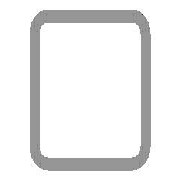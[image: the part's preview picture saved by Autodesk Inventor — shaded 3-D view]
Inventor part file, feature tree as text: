
AUTODESK INVENTOR PART (.ipt)
format: ipt  version: 2025.3 (Build 293356030, 356C)  size: 151,040 bytes
history: native  units: mm (DEFAULTED — no unit token found)
features: other x4, plane x3, split x2, sketch x1
ambient origin geometry x8: Origin, YZ Plane, XZ Plane, XY Plane, X Axis, Y Axis, Z Axis, Center Point
bodies: Solid1 (feature_tree), Body (feature_tree)
feature tree (10):
  parser-record x1  (decoder bookkeeping rows leaked as tree rows — omitted from the tree; the rows remain in map.json)
  other  "Driven Length"
  other  "Start Plane"
  other  "End Plane"
  plane  "Work Plane4"
  split  "Split1"
  plane  "Work Plane5"
  split  "Split2"
  sketch  "Sketch3"  dims[d3=839.332008mm d4=0.0mm d7=4.0mm d9=40.0mm d11=40.0mm d12=2.0mm d13=74.833505mm d14=914.165513mm d15=20.0mm d16=20.0mm d17=90.0deg d18=839.332008mm]
  plane  "Work Plane3"
